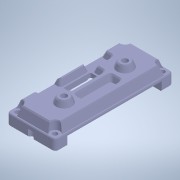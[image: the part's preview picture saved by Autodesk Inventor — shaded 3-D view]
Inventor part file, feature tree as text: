
AUTODESK INVENTOR PART (.ipt)
format: ipt  version: 2021 (Build 250183000, 183)  size: 824,832 bytes
history: native  units: mm
features: projected_geometry x14, sketch x13, extrude x11, chamfer x6, hole x4, fillet x3
ambient origin geometry x8: Origin, YZ Plane, XZ Plane, XY Plane, X Axis, Y Axis, Z Axis, Center Point
bodies: Solid1 (feature_tree)
feature tree (51):
  extrude  "Extrusion1"  Depth=35.25mm
  extrude  "Extrusion2"  Depth=2.75mm TaperAngle=0.0deg
  chamfer  "Chamfer1"  Distance=6.2mm
  hole  "Hole1"  [1 undecoded]
  extrude  "Extrusion3"  Depth=3.2mm
  hole  "Hole4"  [1 undecoded]
  extrude  "Extrusion4"  Depth=4.0mm
  extrude  "Extrusion5"  Depth=5.7mm
  sketch  "Sketch7"  dims[d14=44.0mm d15=3.2mm]
  extrude  "Extrusion6"  TaperAngle=0.0deg  [1 undecoded]
  hole  "Hole2"  [1 undecoded]
  extrude  "Extrusion7"  Depth=4.0mm
  extrude  "Extrusion8"  Depth=77.5mm
  chamfer  "Chamfer2"  Distance=68.0mm
  hole  "Hole3"  [1 undecoded]
  extrude  "Extrusion9"  Depth=4.0mm
  extrude  "Extrusion13"  Depth=4.0mm
  chamfer  "Chamfer3"  Distance=3.5mm
  fillet  "Fillet11"  Radius=2.0mm
  fillet  "Fillet12"  Radius=18.8mm
  fillet  "Fillet13"  Radius=61.0mm
  chamfer  "Chamfer4"  Distance=30.0mm
  chamfer  "Chamfer6"  Distance=30.0mm
  chamfer  "Chamfer7"  Distance=9.0mm
  extrude  "Extrusion14"  Depth=4.0mm
  sketch  "Sketch1"  dims[d0=35.25mm d1=85.25mm]
  sketch  "Sketch2"  dims[d2=2.75mm d3=7.8mm d4=0.0mm]
  projected_geometry  "Projected Loop1"
  sketch  "Sketch3"  dims[d5=1.2mm d6=6.2mm d7=-3.490659mm]
  projected_geometry  "Projected Loop2"
  sketch  "Sketch5"  dims[d8=0.5mm d9=2.0mm d10=45.0deg d13=22.0mm]
  projected_geometry  "Projected Loop3"
  projected_geometry  "Projected Loop4"
  projected_geometry  "Projected Loop5"
  sketch  "Sketch8"  dims[d16=4.2mm d17=6.0mm d18=4.0mm d19=2.0mm d20=90.0deg d21=8.0mm d22=20.594885mm d23=11.3mm]
  sketch  "Sketch9"  dims[d24=11.3mm d25=4.0mm d26=-3.490659mm]
  projected_geometry  "Projected Loop6"
  sketch  "Sketch10"  dims[d28=5.7mm d29=18.2mm]
  projected_geometry  "Projected Loop7"
  sketch  "Sketch11"  dims[d31=7.0mm d32=0.0mm d33=0.0mm]
  projected_geometry  "Projected Loop8"
  sketch  "Sketch12"  dims[d38=4.0mm d39=-3.490659mm d41=13.2mm]
  projected_geometry  "Projected Loop9"
  sketch  "Sketch13"  dims[d47=4.0mm d48=-3.490659mm d54=50.4mm]
  projected_geometry  "Projected Loop10"
  projected_geometry  "Projected Loop11"
  sketch  "Sketch17"  dims[d57=27.0mm d58=77.5mm]
  projected_geometry  "Projected Loop18"
  projected_geometry  "Projected Loop19"
  sketch  "Sketch18"  dims[d59=3.4mm d60=6.0mm d61=6.8mm d62=6.2mm d63=90.0deg d64=5.0mm d65=0.0mm d66=68.0mm d67=6.2mm d68=0.0mm d69=12.6mm d70=12.6mm d71=3.5mm d72=0.0mm d73=0.5mm d74=2.0mm d75=45.0deg d76=18.8mm d77=61.0mm d78=4.0mm d79=6.0mm d80=10.0mm d81=5.7mm d82=90.0deg d83=4.8mm d84=0.0mm d85=30.0mm d86=30.0mm d87=9.0mm d88=24.0mm d89=12.0mm d90=2.0mm d91=2.0mm d92=2.1mm d93=0.0mm d95=8.0mm d96=18.0mm d97=1.7mm d98=10.1mm d99=3.2mm d100=22.0mm d101=44.0mm d102=4.2mm d103=6.0mm d104=4.0mm d105=2.0mm d106=90.0deg d107=8.0mm d108=20.594885mm d109=3.2mm d123=45.0deg d139=4.0mm d140=4.0mm d141=5.0mm d142=0.0mm d143=0.5mm d144=2.0mm d145=45.0deg d146=1.85mm d147=2.0mm d148=1.85mm d149=2.0mm d150=2.0mm d153=2.0mm d154=2.0mm d156=16.4mm d157=11.0mm d158=25.6mm d159=0.5mm d160=0.5mm d161=45.0deg d165=0.5mm d166=2.0mm d167=45.0deg d168=0.5mm d169=2.0mm d170=45.0deg d171=5.5mm d172=9.4mm d173=9.4mm d174=10.9mm d175=10.9mm d178=0.8mm d179=0.0mm d180=7.35mm d181=13.05mm d182=10.1mm d186=4.0mm d187=1.5mm d188=4.0mm d189=1.5mm]
  projected_geometry  "Projected Loop20"
note: 5 required parameter values undecoded (feature->parameter linkage not recoverable at this tier; creation-order binding heuristic only, values carry confidence <= 0.55)
